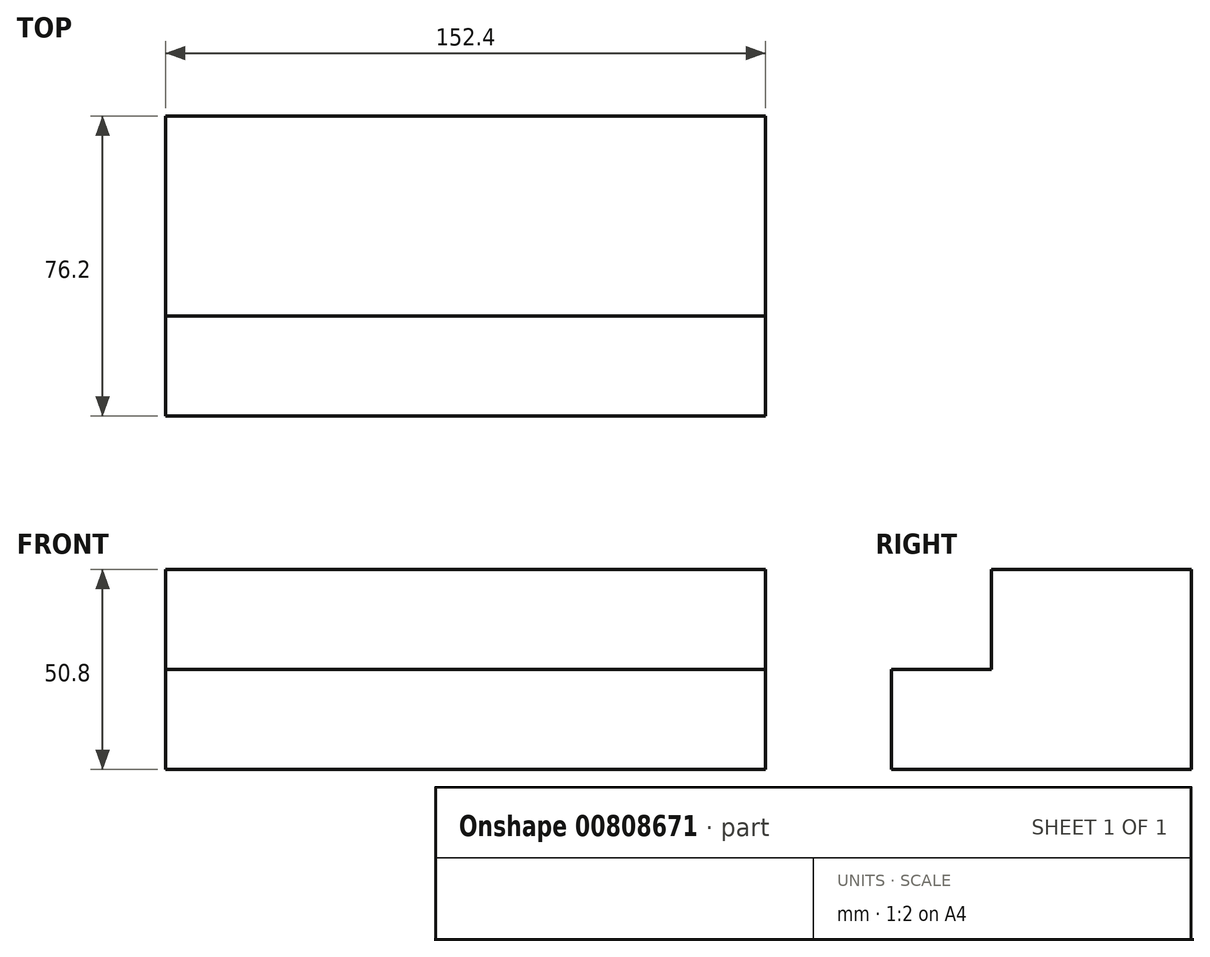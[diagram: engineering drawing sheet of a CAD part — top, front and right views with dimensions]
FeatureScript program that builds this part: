
annotation { "Feature Type Name" : "Feature", "Feature Type Description" : "" }
export const myFeature = defineFeature(function(context is Context, id is Id, definition is map)
    precondition{}
    {
        {
            var Q0;
            Q0=qCreatedBy(makeId("Right.planeOp"),FACE);
            var sketch = newSketch(context, id + "F0", { "sketchPlane" : qUnion([Q0])});
            skLineSegment(sketch, "E0", {"start": v(0, 0) * mm, "end": v(76.2, 0) * mm});
            skLineSegment(sketch, "E1", {"start": v(76.2, 0) * mm, "end": v(76.2, 50.8) * mm});
            skLineSegment(sketch, "E2", {"start": v(76.2, 50.8) * mm, "end": v(25.4, 50.8) * mm});
            skLineSegment(sketch, "E3", {"start": v(25.4, 50.8) * mm, "end": v(25.4, 25.4) * mm});
            skLineSegment(sketch, "E4", {"start": v(25.4, 25.4) * mm, "end": v(0, 25.4) * mm});
            skLineSegment(sketch, "E5", {"start": v(0, 0) * mm, "end": v(0, 25.4) * mm});
            skSolve(sketch);
        }
        {
            var Q0;
            Q0=makeQuery(id+"F0.imprint","IMPRINT",FACE,{"disambiguationData":[TD([[makeQuery(id+"F0.imprint","IMPRINT",EDGE,{"derivedFrom":sQuery(id+"F0.wireOp",EDGE,"E0")}),1.0]])]});
            extrude(context, id + "F1", {"entities" : qUnion([Q0]), "depth" : 152.4 * mm, "offsetDistance" : 25.4 * mm});
        }
    });
